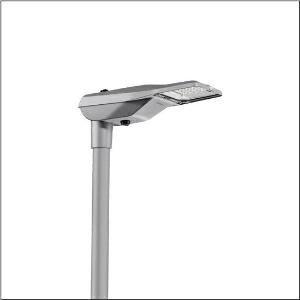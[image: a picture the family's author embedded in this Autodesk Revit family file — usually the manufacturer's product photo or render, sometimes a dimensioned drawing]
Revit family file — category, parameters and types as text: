
# Revit family: streetlight_sl_21_micro___st1_0a_5xe1d33t08db_ddb2
name_source: partatom
category: Lighting Fixtures
units: mm (PartAtom-declared; Revit-internal decimal feet)

## family parameters
Cut with Voids When Loaded = No
Host = Face
Light Source = No
Part Type = Normal
Room Calculation Point = No
Round Connector Dimension = Use Diameter
Shared = No

## types (1)
- --- (1 x LED, 5110 lm, 39.1 W, 3000K)
    Apparent Load = 39 VA
    CIE Flux Codes = 37 72 97 100 100
    Color Rendering = 70
    Color Temperature = 3000K
    Default Elevation = 1800 mm
    Description = Streetlight SL 21 micro, mast luminaire, primary light control with lens, of PMMA, primary optical cover: cover, of toughened safety glass, transparent, light distribution: ST1.0a, light emission: direct distribution, primary light characteristic: asymmetric, installation type: side-entry, post-top, LED, High Power LED, rated luminous flux: 5.110lm, luminous efficacy: 131lm/W, light colour: 730, colour temperature: 3000K, control gear: D4i, control: flexible luminous flux parameterisation, time-dependent luminous flux control, constant luminous flux control, overheat protection, pre-setting: logarithmic dimming characteristic, mains connection: 220..240V, AC, 50/60Hz, start of lifetime: 39W, end of service life: 41W, reduction: 18W, luminaire housing, of diecast aluminium, powder-coated, SITECO metallic grey (DB 702S), corrosivity category C5 high according to DIN EN ISO 12944, please order mast flange separately, inclination adjustable: 0°, 5°, 10°, 15°, sealing non-destructively replaceable, multi-level sealing system, length: 528mm, width: 235mm, height: 110mm, mast flange for spigot size: 42mm (side-entry): 5XC10008XM4, 60/48mm (side-entry/post-top): 5XC10108XM2, 76/60mm (side-entry/post-top): 5XC10108XM1, Smart Interface below and above, protection rating (complete): IP66, insulation class (complete): insulation class II (safety insulation), certification: CE, ENEC, ENEC+, VDE, impact resistance: IK10, permissible operating ambient temperature for outdoor applications: -40..+50°C, standard-compliant lighting for roads and squares, packaging unit: 1 piece

Light Distribution: ST1.0a
    Height = 110 mm
    Lamp = 1 x LED
    Lamp Light Flux = 5110 lm
    Lamp Power = 39.1 W
    Lamp count = 1
    Length = 528 mm
    Luminous efficacy = 131 lm/W
    Manufacturer = Siteco
    ModVariant = No
    Model = 5XE1D33T08DB
    Mounting Place = Pole
    Mounting Type = Pole top
    Number of Poles = 1
    OnlyDefault = Yes
    Power Factor = 1
    Product Name = Streetlight SL 21 micro | ST1.0a
    Product group = mast luminaire | pylon top
    ProductGroupID = 6100
    Protection Class = Protection class II
    Protection Degree = IP 66
    RLX_Detail_Level = 1
    RLX_Emergency_Light_Flux = 0 lm
    RLX_Emergency_Type = 0
    RLX_Emergency_Type_DB = No
    RlxData = <blob elided: 98757 chars, md5=af36b7ce>
    Socket = socket
    Standby Power = 0 W
    System Light Flux = 5110 lm
    System Power = 39 W
    Type Comments = factory setting: luminous flux: 100 % | dim-lin: 254 | 765 mA
    Type Image = l_1007239.jpg
    URL = http://relux.com
    VarID = @adj_156807
    Voltage = 0 V
    Weight = 0.00 kg
    Width = 235 mm

## geometry (parser evidence)
native form markers: Blend x4, Sweep x9
no freeform markers — native parametric forms only
